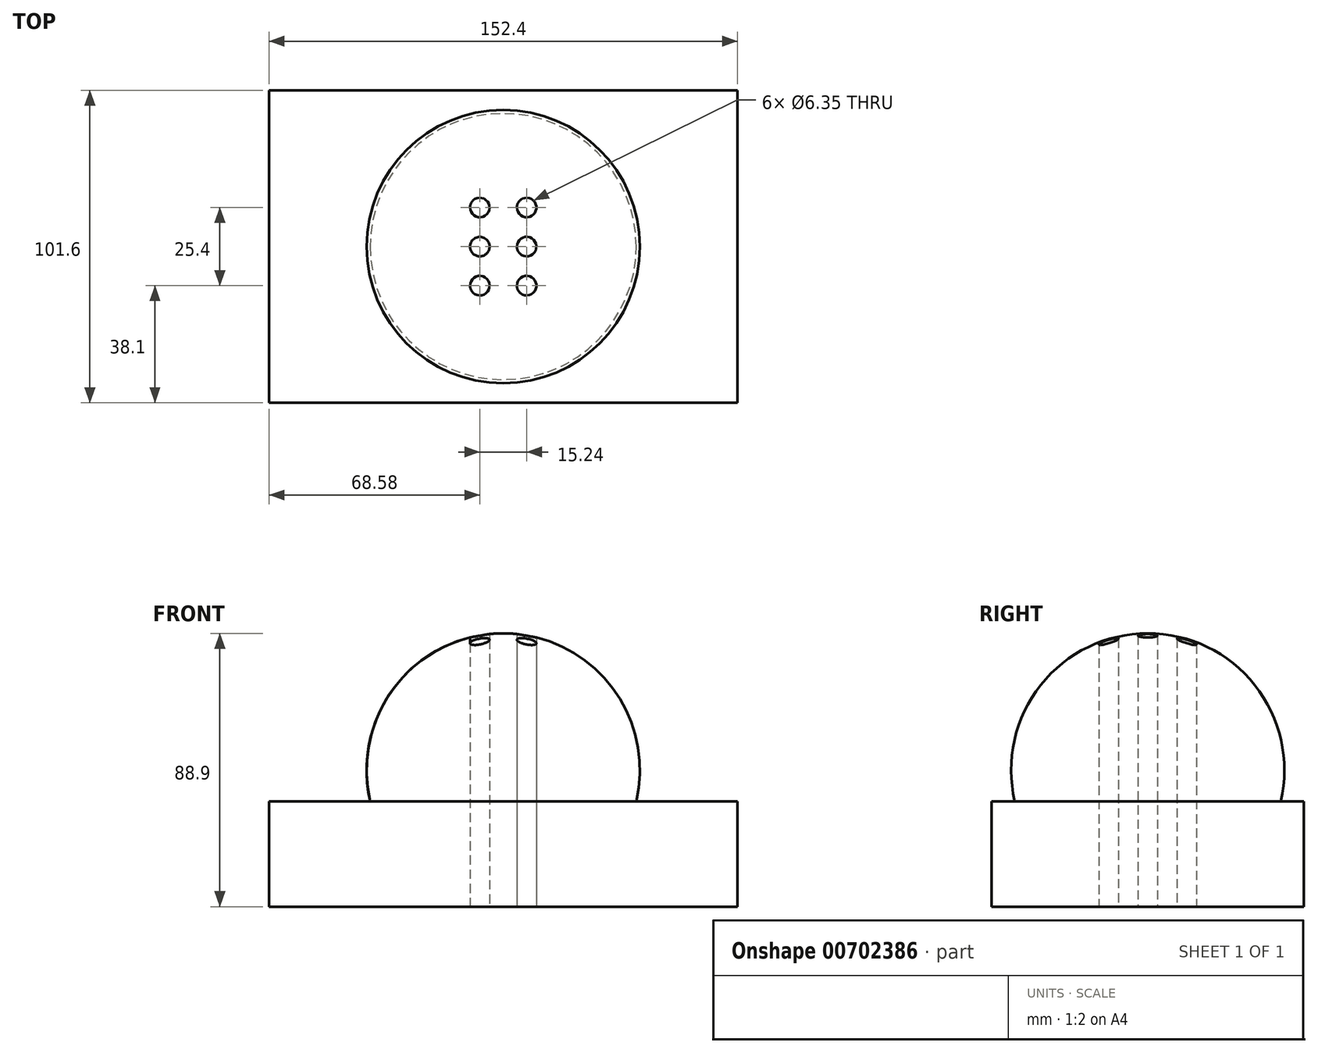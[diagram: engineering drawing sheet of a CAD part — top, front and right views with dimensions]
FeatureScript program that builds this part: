
annotation { "Feature Type Name" : "Feature", "Feature Type Description" : "" }
export const myFeature = defineFeature(function(context is Context, id is Id, definition is map)
    precondition{}
    {
        {
            var Q0;
            Q0=qCreatedBy(makeId("Top.planeOp"),FACE);
            var sketch = newSketch(context, id + "F0", { "sketchPlane" : qUnion([Q0])});
            skLineSegment(sketch, "E0.bottom", {"start": v(76.2, -50.8) * mm, "end": v(-76.2, -50.8) * mm});
            skLineSegment(sketch, "E0.top", {"start": v(76.2, 50.8) * mm, "end": v(-76.2, 50.8) * mm});
            skLineSegment(sketch, "E0.left", {"start": v(76.2, -50.8) * mm, "end": v(76.2, 50.8) * mm});
            skLineSegment(sketch, "E0.right", {"start": v(-76.2, -50.8) * mm, "end": v(-76.2, 50.8) * mm});
            skPoint(sketch, "E0.middle", {"position": v(0, 0) * mm});
            skSolve(sketch);
        }
        {
            var Q0;
            Q0=makeQuery(id+"F0.imprint","IMPRINT",FACE,{"disambiguationData":[TD([[makeQuery(id+"F0.imprint","IMPRINT",EDGE,{"derivedFrom":sQuery(id+"F0.wireOp",EDGE,"E0.bottom")}),-1.0]])]});
            extrude(context, id + "F1", {"entities" : qUnion([Q0]), "depth" : 34.3 * mm, "offsetDistance" : 25.4 * mm});
        }
        {
            var Q0;
            Q0=qCreatedBy(makeId("Front.planeOp"),FACE);
            var sketch = newSketch(context, id + "F2", { "sketchPlane" : qUnion([Q0])});
            skLineSegment(sketch, "E1", {"start": v(0, 0) * mm, "end": v(0, 88.9) * mm});
            skArc(sketch, "E2", {"start": v(0, 0) * mm, "mid": v(44.45, 44.45) * mm, "end": v(0, 88.9) * mm});
            skSolve(sketch);
        }
        {
            var Q0;
            Q0 = qSketchRegion(id + "F2", true);
            var Q1;
            Q1=sQuery(id+"F2.wireOp",EDGE,"E1");
            revolve(context, id + "F3", {"operationType" : NewBodyOperationType.ADD, "surfaceOperationType" : NewSurfaceOperationType.NEW, "entities" : qUnion([Q0]), "axis" : qUnion([Q1]), "revolveType" : RevolveType.FULL});
        }
        {
            var Q0;
            Q0=qCreatedBy(makeId("Top.planeOp"),FACE);
            var sketch = newSketch(context, id + "F4", { "sketchPlane" : qUnion([Q0])});
            skCircle(sketch, "E3", {"center": v(-7.62, 0) * mm, "radius": 1.17 * mm});
            skCircle(sketch, "E4", {"center": v(7.62, 0) * mm, "radius": 1.03 * mm});
            skCircle(sketch, "E5", {"center": v(7.62, 12.7) * mm, "radius": 3.18 * mm});
            skCircle(sketch, "E6", {"center": v(7.62, -12.7) * mm, "radius": 3.18 * mm});
            skCircle(sketch, "E7", {"center": v(-7.62, -12.7) * mm, "radius": 3.18 * mm});
            skCircle(sketch, "E8", {"center": v(-7.62, 12.7) * mm, "radius": 3.18 * mm});
            skCircle(sketch, "E9", {"center": v(-7.62, 0) * mm, "radius": 3.18 * mm});
            skCircle(sketch, "E10", {"center": v(7.62, 0) * mm, "radius": 3.18 * mm});
            skSolve(sketch);
        }
        {
            var Q0;
            Q0=sQuery(id+"F4.wireOp",VERTEX,"E8.center");
            var Q1;
            Q1=sQuery(id+"F4.wireOp",VERTEX,"E5.center");
            var Q2;
            Q2=sQuery(id+"F4.wireOp",VERTEX,"E9.center");
            var Q3;
            Q3=sQuery(id+"F4.wireOp",VERTEX,"E6.center");
            var Q4;
            Q4=sQuery(id+"F4.wireOp",VERTEX,"E7.center");
            var Q5;
            Q5=sQuery(id+"F4.wireOp",VERTEX,"E4.center");
            var Q6;
            Q6=makeQuery(id+"F1.opExtrude","SWEPT_BODY",BODY,{"disambiguationData":[OSD([sQuery(id+"F0.wireOp",EDGE,"E0.bottom"),sQuery(id+"F0.wireOp",EDGE,"E0.top"),sQuery(id+"F0.wireOp",EDGE,"E0.left"),sQuery(id+"F0.wireOp",EDGE,"E0.right")])]});
            hole(context, id + "F5", {"style" : HoleStyle.SIMPLE, "endStyle" : HoleEndStyle.THROUGH, "oppositeDirection" : true, "holeDiameter" : 6.35 * mm, "majorDiameter" : 6.35 * mm, "isTappedThrough" : true, "tappedDepth" : 12.7 * mm, "tapClearance" : 3, "locations" : qUnion([Q0, Q1, Q2, Q3, Q4, Q5]), "scope" : qUnion([Q6])});
        }
    });
